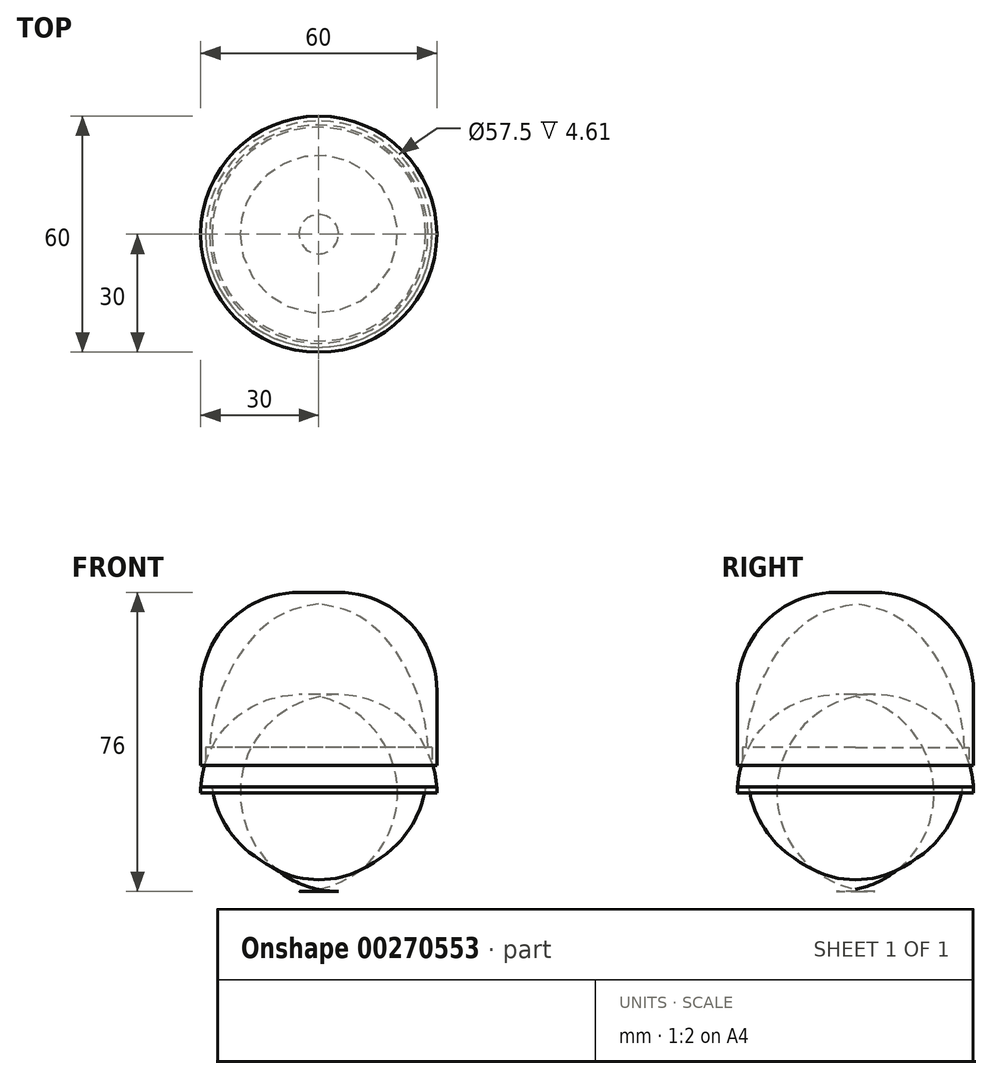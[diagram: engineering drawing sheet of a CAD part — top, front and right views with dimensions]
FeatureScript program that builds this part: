
annotation { "Feature Type Name" : "Feature", "Feature Type Description" : "" }
export const myFeature = defineFeature(function(context is Context, id is Id, definition is map)
    precondition{}
    {
        {
            var Q0;
            Q0=qCreatedBy(makeId("Front.planeOp"),FACE);
            var sketch = newSketch(context, id + "F0", { "sketchPlane" : qUnion([Q0])});
            skFitSpline(sketch, "E0", {"points": [v(0, 46.43) * mm, v(-8.86, 44.14) * mm, v(-16.29, 38.43) * mm, v(-20.86, 32.43) * mm, v(-25.14, 23.29) * mm, v(-27.43, 13.57) * mm, v(-27.71, 6.14) * mm, v(-26.29, -3.86) * mm, v(-22, -12.14) * mm, v(-16, -17.86) * mm, v(-6.57, -22.71) * mm, v(0, -23.57) * mm], "startDerivative": vector(-98.81, -15.48) * mm, "endDerivative": vector(79.6, -2.58) * mm});
            skLineSegment(sketch, "E1", {"start": v(0, 46.43) * mm, "end": v(0, -23.57) * mm});
            skPoint(sketch, "E2", {"position": v(-27.68, 5.4) * mm});
            skLineSegment(sketch, "E3", {"start": v(-30, 48.2) * mm, "end": v(-30, 5.4) * mm});
            skLineSegment(sketch, "E4", {"start": v(-30, -21.8) * mm, "end": v(-30, 2.4) * mm});
            skLineSegment(sketch, "E5", {"start": v(0, 46.43) * mm, "end": v(0, 49.43) * mm});
            skLineSegment(sketch, "E6", {"start": v(0, 49.43) * mm, "end": v(-30, 49.43) * mm});
            skLineSegment(sketch, "E7", {"start": v(-30, 49.43) * mm, "end": v(-30, 48.2) * mm});
            skLineSegment(sketch, "E8", {"start": v(0, -23.57) * mm, "end": v(0, -26.57) * mm});
            skLineSegment(sketch, "E9", {"start": v(0, -26.57) * mm, "end": v(-30, -26.57) * mm});
            skLineSegment(sketch, "E10", {"start": v(-30, -26.57) * mm, "end": v(-30, -21.8) * mm});
            skLineSegment(sketch, "E11", {"start": v(-30, 2.4) * mm, "end": v(-27.46, 2.4) * mm});
            skLineSegment(sketch, "E12", {"start": v(-30, 5.4) * mm, "end": v(-27.68, 5.4) * mm});
            skSolve(sketch);
        }
        {
            var Q0;
            Q0=makeQuery(id+"F0.imprint","IMPRINT",FACE,{"disambiguationData":[TD([[makeQuery(id+"F0.imprint","IMPRINT",EDGE,{"derivedFrom":sQuery(id+"F0.wireOp",EDGE,"E3")}),1.0]])]});
            var Q1;
            Q1=sQuery(id+"F0.wireOp",EDGE,"E1");
            revolve(context, id + "F1", {"entities" : qUnion([Q0]), "axis" : qUnion([Q1]), "revolveType" : RevolveType.FULL});
        }
        {
            var Q0;
            Q0=makeQuery(id+"F1.opRevolve","SWEPT_EDGE",EDGE,{"disambiguationData":[OSD([sQuery(id+"F0.wireOp",EDGE,"E6"),sQuery(id+"F0.wireOp",EDGE,"E7")])]});
            fillet(context, id + "F2", {"entities" : qUnion([Q0]), "radius" : 25 * mm, "tangentPropagation" : true, "allowEdgeOverflow" : false});
        }
        {
            var Q0;
            Q0=makeQuery(id+"F0.imprint","IMPRINT",FACE,{"disambiguationData":[TD([[makeQuery(id+"F0.imprint","IMPRINT",EDGE,{"derivedFrom":sQuery(id+"F0.wireOp",EDGE,"E4")}),-1.0]])]});
            var Q1;
            Q1=sQuery(id+"F0.wireOp",EDGE,"E1");
            revolve(context, id + "F3", {"entities" : qUnion([Q0]), "axis" : qUnion([Q1]), "revolveType" : RevolveType.FULL});
        }
        {
            var Q0;
            Q0=makeQuery(id+"F3.opRevolve","SWEPT_EDGE",EDGE,{"disambiguationData":[OSD([sQuery(id+"F0.wireOp",EDGE,"E9"),sQuery(id+"F0.wireOp",EDGE,"E10")])]});
            fillet(context, id + "F4", {"entities" : qUnion([Q0]), "radius" : 25 * mm, "tangentPropagation" : true, "allowEdgeOverflow" : false});
        }
        {
            var Q0;
            Q0=qCreatedBy(makeId("Top.planeOp"),FACE);
            var sketch = newSketch(context, id + "F5", { "sketchPlane" : qUnion([Q0])});
            skLineSegment(sketch, "E13", {"start": v(0, 0) * mm, "end": v(28.75, 0) * mm, "construction": true});
            skLineSegment(sketch, "E14", {"start": v(0, 0) * mm, "end": v(-28.75, 0) * mm, "construction": true});
            skLineSegment(sketch, "E15", {"start": v(0, 0) * mm, "end": v(0, 28.75) * mm, "construction": true});
            skLineSegment(sketch, "E16", {"start": v(0, 0) * mm, "end": v(0, -28.75) * mm, "construction": true});
            skCircle(sketch, "E17", {"center": v(0, 0) * mm, "radius": 28.75 * mm});
            skCircle(sketch, "E18", {"center": v(0, 0) * mm, "radius": 30 * mm});
            skSolve(sketch);
        }
        {
            var Q0;
            Q0=makeQuery(id+"F5.imprint","IMPRINT",FACE,{"disambiguationData":[TD([[makeQuery(id+"F5.imprint","IMPRINT",EDGE,{"derivedFrom":sQuery(id+"F5.wireOp",EDGE,"E17")}),1.0]])]});
            extrude(context, id + "F6", {"entities" : qUnion([Q0]), "operationType" : NewBodyOperationType.REMOVE, "depth" : 10 * mm});
        }
        {
            var Q0;
            Q0=makeQuery(id+"F5.imprint","IMPRINT",FACE,{"disambiguationData":[TD([[makeQuery(id+"F5.imprint","IMPRINT",EDGE,{"derivedFrom":sQuery(id+"F5.wireOp",EDGE,"E17")}),-1.0]])]});
            extrude(context, id + "F7", {"entities" : qUnion([Q0]), "operationType" : NewBodyOperationType.REMOVE, "depth" : 3 * mm});
        }
    });
